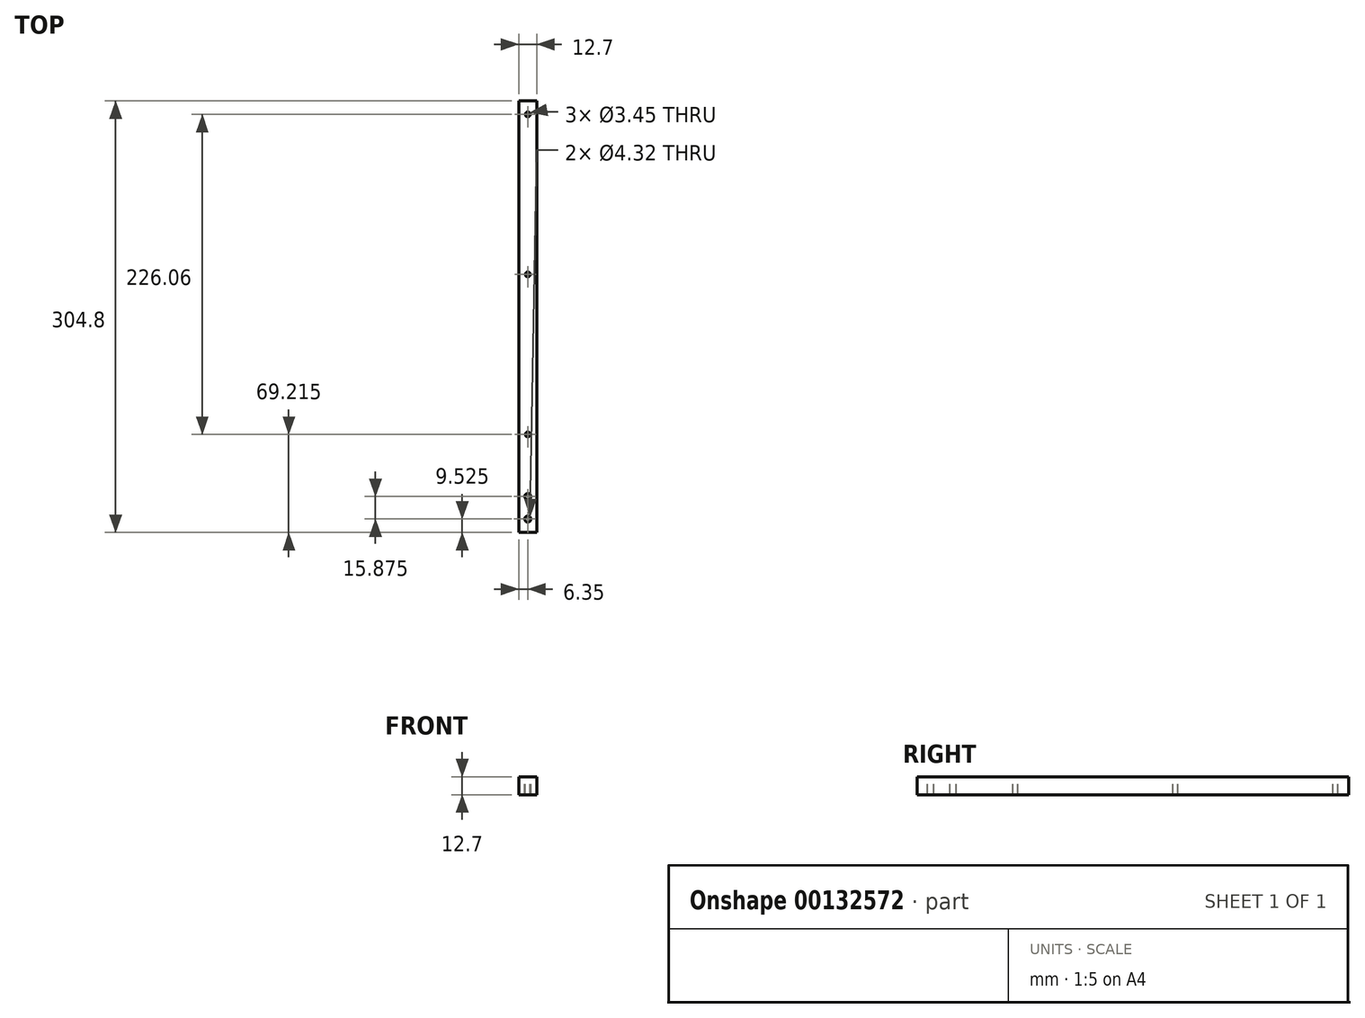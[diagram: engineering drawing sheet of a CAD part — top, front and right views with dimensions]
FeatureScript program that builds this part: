
annotation { "Feature Type Name" : "Feature", "Feature Type Description" : "" }
export const myFeature = defineFeature(function(context is Context, id is Id, definition is map)
    precondition{}
    {
        {
            var Q0;
            Q0=qCreatedBy(makeId("Front.planeOp"),FACE);
            var sketch = newSketch(context, id + "F0", { "sketchPlane" : qUnion([Q0])});
            skLineSegment(sketch, "E0.bottom", {"start": v(0, 0) * mm, "end": v(12.7, 0) * mm});
            skLineSegment(sketch, "E0.top", {"start": v(0, 12.7) * mm, "end": v(12.7, 12.7) * mm});
            skLineSegment(sketch, "E0.left", {"start": v(0, 0) * mm, "end": v(0, 12.7) * mm});
            skLineSegment(sketch, "E0.right", {"start": v(12.7, 0) * mm, "end": v(12.7, 12.7) * mm});
            skSolve(sketch);
        }
        {
            var Q0;
            Q0=makeQuery(id+"F0.imprint","IMPRINT",FACE,{"disambiguationData":[TD([[makeQuery(id+"F0.imprint","IMPRINT",EDGE,{"derivedFrom":sQuery(id+"F0.wireOp",EDGE,"E0.bottom")}),1.0]])]});
            extrude(context, id + "F1", {"entities" : qUnion([Q0]), "depth" : 304.8 * mm});
        }
        {
            var Q0;
            Q0=makeQuery(id+"F1.opExtrude","SWEPT_FACE",FACE,{"disambiguationData":[OSD([sQuery(id+"F0.wireOp",EDGE,"E0.top")])]});
            var sketch = newSketch(context, id + "F2", { "sketchPlane" : qUnion([Q0])});
            skPoint(sketch, "E1", {"position": v(6.35, -9.53) * mm});
            skPoint(sketch, "E1.positionSnap0", {"position": v(6.35, 0) * mm});
            skPoint(sketch, "E2", {"position": v(6.35, -122.56) * mm});
            skPoint(sketch, "E3", {"position": v(6.35, -235.59) * mm});
            skPoint(sketch, "E4", {"position": v(6.35, -295.28) * mm});
            skPoint(sketch, "E4.positionSnap0", {"position": v(6.35, -304.8) * mm});
            skPoint(sketch, "E5", {"position": v(6.35, -279.4) * mm});
            skSolve(sketch);
        }
        {
            var Q0;
            Q0=sQuery(id+"F2.wireOp",VERTEX,"E1");
            var Q1;
            Q1=sQuery(id+"F2.wireOp",VERTEX,"E2");
            var Q2;
            Q2=sQuery(id+"F2.wireOp",VERTEX,"E3");
            var Q3;
            Q3=makeQuery(id+"F1.opExtrude","SWEPT_BODY",BODY,{"disambiguationData":[OSD([sQuery(id+"F0.wireOp",EDGE,"E0.bottom"),sQuery(id+"F0.wireOp",EDGE,"E0.top"),sQuery(id+"F0.wireOp",EDGE,"E0.left"),sQuery(id+"F0.wireOp",EDGE,"E0.right")])]});
            hole(context, id + "F3", {"style" : HoleStyle.SIMPLE, "endStyle" : HoleEndStyle.THROUGH, "standardTappedOrClearance" : lookupTablePath({ "standard" : "ANSI", "engagement" : "75%", "pitch" : "32 tpi", "size" : "#8", "type" : "Tapped" }), "standardBlindInLast" : lookupTablePath({ "standard" : "ANSI", "engagement" : "75%", "pitch" : "32 tpi", "size" : "#8", "type" : "Tapped" }), "holeDiameter" : 3.45 * mm, "locations" : qUnion([Q0, Q1, Q2]), "scope" : qUnion([Q3]), "isTappedThrough" : true, "majorDiameter" : 4.17 * mm, "showTappedDepth" : true});
        }
        {
            var Q0;
            Q0=makeQuery(id+"F1.opExtrude","SWEPT_FACE",FACE,{"disambiguationData":[OSD([sQuery(id+"F0.wireOp",EDGE,"E0.top")])]});
            var sketch = newSketch(context, id + "F4", { "sketchPlane" : qUnion([Q0])});
            skPoint(sketch, "E6", {"position": v(6.35, -9.53) * mm});
            skPoint(sketch, "E6.positionSnap0", {"position": v(6.35, 0) * mm});
            skPoint(sketch, "E7", {"position": v(6.35, -122.56) * mm});
            skPoint(sketch, "E8", {"position": v(6.35, -235.59) * mm});
            skPoint(sketch, "E9", {"position": v(6.35, -295.28) * mm});
            skPoint(sketch, "E9.positionSnap0", {"position": v(6.35, -304.8) * mm});
            skPoint(sketch, "E10", {"position": v(6.35, -279.4) * mm});
            skSolve(sketch);
        }
        {
            var Q0;
            Q0=sQuery(id+"F4.wireOp",VERTEX,"E9");
            var Q1;
            Q1=sQuery(id+"F4.wireOp",VERTEX,"E10");
            var Q2;
            Q2=makeQuery(id+"F1.opExtrude","SWEPT_BODY",BODY,{"disambiguationData":[OSD([sQuery(id+"F0.wireOp",EDGE,"E0.bottom"),sQuery(id+"F0.wireOp",EDGE,"E0.top"),sQuery(id+"F0.wireOp",EDGE,"E0.left"),sQuery(id+"F0.wireOp",EDGE,"E0.right")])]});
            hole(context, id + "F5", {"style" : HoleStyle.SIMPLE, "endStyle" : HoleEndStyle.THROUGH, "standardTappedOrClearance" : lookupTablePath({ "standard" : "ANSI", "fit" : "Close", "size" : "#8", "type" : "Clearance" }), "standardBlindInLast" : lookupTablePath({ "fit" : "Close", "standard" : "ANSI", "size" : "#8", "type" : "Clearance" }), "holeDiameter" : 4.32 * mm, "locations" : qUnion([Q0, Q1]), "scope" : qUnion([Q2]), "isTappedThrough" : true});
        }
    });
